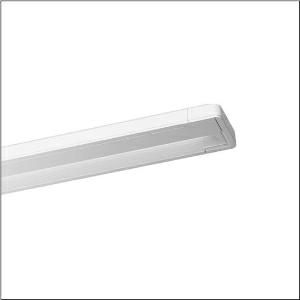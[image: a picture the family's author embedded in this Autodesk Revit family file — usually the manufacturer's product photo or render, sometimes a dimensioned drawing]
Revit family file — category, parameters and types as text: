
# Revit family: taris_r__21_5mt226d04wa_9895
name_source: partatom
category: Lighting Fixtures
units: mm (PartAtom-declared; Revit-internal decimal feet)

## family parameters
Cut with Voids When Loaded = No
Host = Face
Light Source = No
Part Type = Normal
Room Calculation Point = No
Round Connector Dimension = Use Diameter
Shared = No

## types (1)
- --- (1 x LED, 4080 lm, 28.9 W, 4000K)
    Apparent Load = 29 VA
    CIE Flux Codes = 66 91 98 100 100
    Color Rendering = 80
    Color Temperature = 4000K
    Default Elevation = 1800 mm
    Description = Taris® 21, office luminaire, primary light control with wallwasher, primary anti-glare with micro louvre, primary optical cover: axial lens, of PMMA, structured, light emission: direct distribution, primary light characteristic: asymmetric, installation type: surface-mounted, LED, rated luminous flux: 4.080lm, luminous efficacy: 141lm/W, light colour: 840, colour temperature: 4000K, control gear: ECG DALI, with terminal, 5-pole, mains connection: 230V, AC, 50Hz, rated input power: 29W, luminaire housing, of plastic, traffic white (RAL 9016), length: 1.230mm, width: 134mm, height: 50mm, protection rating (complete): IP20, insulation class (complete): insulation class I (protective earthing), certification: CE, protection symbol: F, impact resistance: IK02, permissible operating ambient temperature: 0..+35°C, standard: EN 50419, packaging unit: 1 piece
    Height = 51 mm
    Lamp = 1 x LED
    Lamp Light Flux = 4080 lm
    Lamp Power = 28.9 W
    Lamp count = 1
    Length = 1233 mm
    Luminous efficacy = 141 lm/W
    Manufacturer = Siteco
    ModVariant = No
    Model = 5MT226D04WA
    Mounting Place = Ceiling
    Mounting Type = Surface mounted
    Number of Poles = 1
    OnlyDefault = Yes
    Power Factor = 1
    Product Name = Taris® 21
    Product group = office luminaire | ceiling mounted
    ProductGroupID = 304
    Protection Class = Protection class I
    Protection Degree = IP 20
    RLX_Detail_Level = 1
    RLX_Emergency_Light_Flux = 0 lm
    RLX_Emergency_Type = 0
    RLX_Emergency_Type_DB = No
    RlxData = <blob elided: 41897 chars, md5=3f7c5709>
    Socket = socket
    Standby Power = 0 W
    System Light Flux = 4080 lm
    System Power = 29 W
    Type Comments = factory setting: luminous flux: 100 % | dim-lin: 254 | 200 mA
    Type Image = l_1004726.jpg
    URL = http://relux.com
    VarID = @adj_136933
    Voltage = 0 V
    Weight = 0.00 kg
    Width = 134 mm

## geometry (parser evidence)
native form markers: Blend x4, Sweep x8
no freeform markers — native parametric forms only
